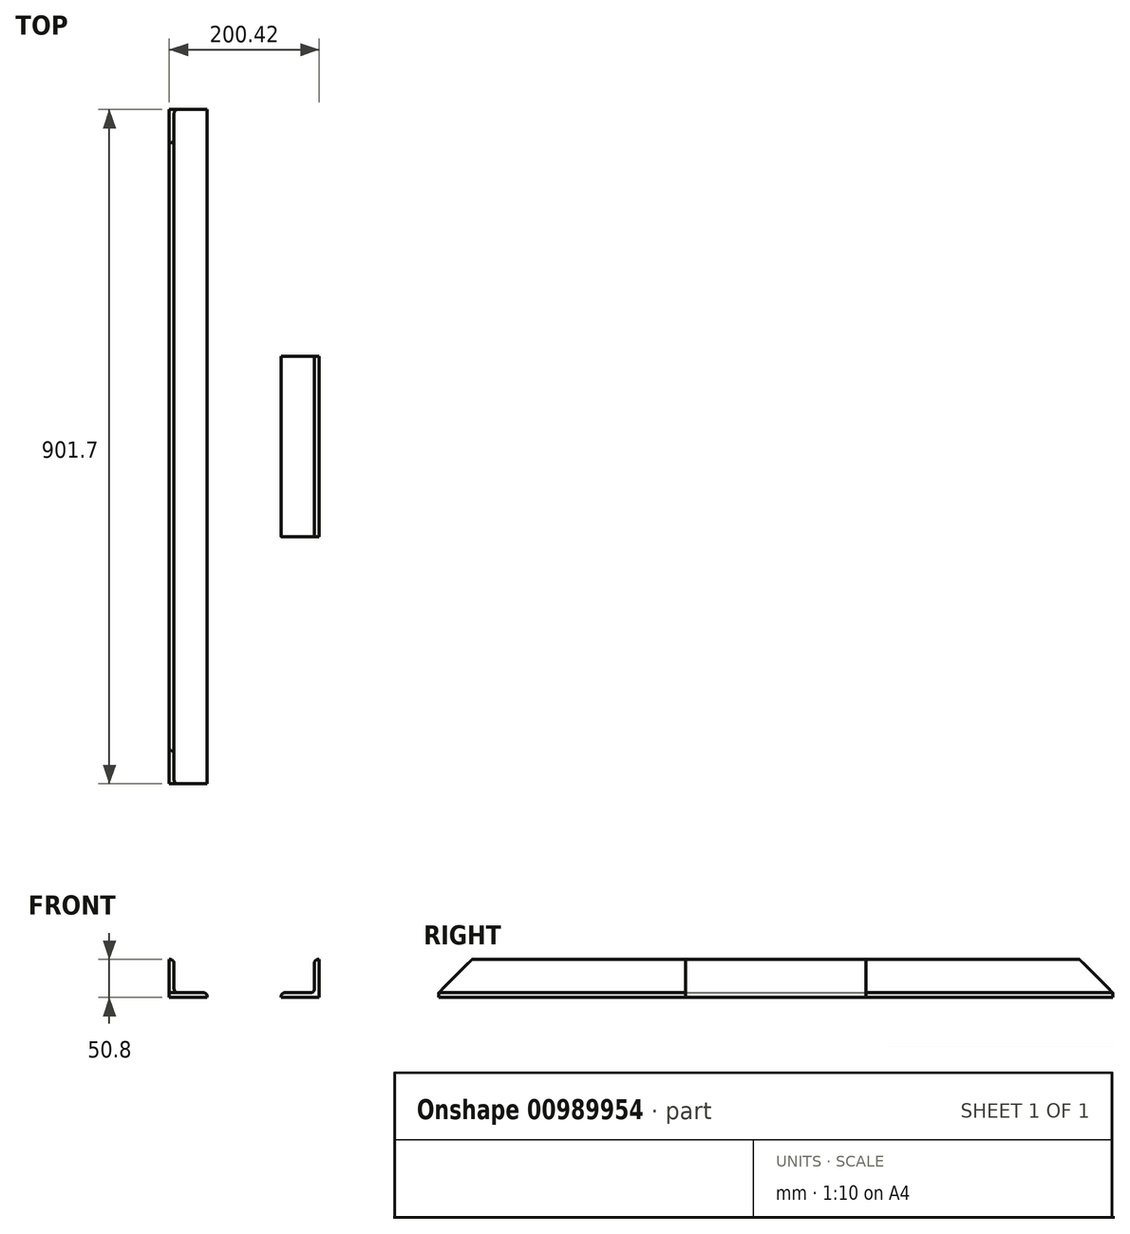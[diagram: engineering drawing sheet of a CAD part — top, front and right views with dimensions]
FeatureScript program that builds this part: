
annotation { "Feature Type Name" : "Feature", "Feature Type Description" : "" }
export const myFeature = defineFeature(function(context is Context, id is Id, definition is map)
    precondition{}
    {
        {
            var Q0;
            Q0=qCreatedBy(makeId("Front.planeOp"),FACE);
            var sketch = newSketch(context, id + "F0", { "sketchPlane" : qUnion([Q0])});
            skLineSegment(sketch, "E0.bottom", {"start": v(25.4, -25.4) * mm, "end": v(-25.4, -25.4) * mm});
            skLineSegment(sketch, "E0.top", {"start": v(-19.05, 25.4) * mm, "end": v(-25.4, 25.4) * mm});
            skLineSegment(sketch, "E0.left", {"start": v(25.4, -25.4) * mm, "end": v(25.4, -19.05) * mm});
            skLineSegment(sketch, "E0.right", {"start": v(-25.4, -25.4) * mm, "end": v(-25.4, 25.4) * mm});
            skPoint(sketch, "E0.middle", {"position": v(0, 0) * mm});
            skLineSegment(sketch, "E1.0", {"start": v(-19.05, -19.05) * mm, "end": v(-19.05, 25.4) * mm});
            skLineSegment(sketch, "E2.0", {"start": v(25.4, -19.05) * mm, "end": v(-19.05, -19.05) * mm});
            skPoint(sketch, "E3.orphan", {"position": v(25.4, 25.4) * mm});
            skLineSegment(sketch, "E4", {"start": v(74.8, 75.28) * mm, "end": v(74.8, -68.93) * mm});
            skLineSegment(sketch, "E5.MirrorCS", {"start": v(168.67, 25.4) * mm, "end": v(175.02, 25.4) * mm});
            skLineSegment(sketch, "E6.MirrorCS", {"start": v(124.22, -25.4) * mm, "end": v(124.22, -19.05) * mm});
            skPoint(sketch, "E7.MirrorP", {"position": v(124.22, 25.4) * mm});
            skLineSegment(sketch, "E8.MirrorCS", {"start": v(124.22, -25.4) * mm, "end": v(175.02, -25.4) * mm});
            skLineSegment(sketch, "E9.MirrorCS", {"start": v(168.67, -19.05) * mm, "end": v(168.67, 25.4) * mm});
            skLineSegment(sketch, "E10.MirrorCS", {"start": v(124.22, -19.05) * mm, "end": v(168.67, -19.05) * mm});
            skLineSegment(sketch, "E11.MirrorCS", {"start": v(175.02, -25.4) * mm, "end": v(175.02, 25.4) * mm});
            skPoint(sketch, "E12.MirrorP", {"position": v(149.62, 0) * mm});
            skSolve(sketch);
        }
        {
            var Q0;
            Q0=makeQuery(id+"F0.imprint","IMPRINT",FACE,{"disambiguationData":[TD([[makeQuery(id+"F0.imprint","IMPRINT",EDGE,{"derivedFrom":sQuery(id+"F0.wireOp",EDGE,"E0.bottom")}),-1.0]])]});
            extrude(context, id + "F1", {"entities" : qUnion([Q0]), "endBound" : BoundingType.SYMMETRIC, "depth" : 901.7 * mm, "offsetDistance" : 25.4 * mm});
        }
        {
            var Q0;
            Q0=makeQuery(id+"F0.imprint","IMPRINT",FACE,{"disambiguationData":[TD([[makeQuery(id+"F0.imprint","IMPRINT",EDGE,{"derivedFrom":sQuery(id+"F0.wireOp",EDGE,"E5.MirrorCS")}),-1.0]])]});
            extrude(context, id + "F2", {"entities" : qUnion([Q0]), "endBound" : BoundingType.SYMMETRIC, "depth" : 241.3 * mm, "offsetDistance" : 25.4 * mm});
        }
        {
            var Q0;
            Q0=makeQuery(id+"F1.opExtrude","SWEPT_FACE",FACE,{"disambiguationData":[OSD([sQuery(id+"F0.wireOp",EDGE,"E1.0")])]});
            var sketch = newSketch(context, id + "F3", { "sketchPlane" : qUnion([Q0])});
            skPoint(sketch, "E13.0", {"position": v(-450.85, -19.05) * mm});
            skPoint(sketch, "E14.0", {"position": v(-450.85, 25.4) * mm});
            skLineSegment(sketch, "E15", {"start": v(-450.85, -19.05) * mm, "end": v(-450.85, 25.4) * mm});
            skLineSegment(sketch, "E16", {"start": v(-450.85, 25.4) * mm, "end": v(-406.4, 25.4) * mm});
            skLineSegment(sketch, "E17", {"start": v(-406.4, 25.4) * mm, "end": v(-450.85, -19.05) * mm});
            skLineSegment(sketch, "E18.MirrorCS", {"start": v(406.4, 25.4) * mm, "end": v(450.85, -19.05) * mm});
            skLineSegment(sketch, "E19.MirrorCS", {"start": v(450.85, 25.4) * mm, "end": v(406.4, 25.4) * mm});
            skLineSegment(sketch, "E20.MirrorCS", {"start": v(450.85, -19.05) * mm, "end": v(450.85, 25.4) * mm});
            skSolve(sketch);
        }
        {
            var Q0;
            Q0 = qSketchRegion(id + "F3", true);
            extrude(context, id + "F4", {"entities" : qUnion([Q0]), "operationType" : NewBodyOperationType.REMOVE, "oppositeDirection" : true, "depth" : 25.4 * mm, "offsetDistance" : 25.4 * mm});
        }
        {
            var Q0;
            Q0=makeQuery(id+"F1.opExtrude","SWEPT_EDGE",EDGE,{"disambiguationData":[OSD([sQuery(id+"F0.wireOp",EDGE,"E1.0"),sQuery(id+"F0.wireOp",EDGE,"E2.0")])]});
            var Q1;
            Q1=makeQuery(id+"F1.opExtrude","SWEPT_EDGE",EDGE,{"disambiguationData":[OSD([sQuery(id+"F0.wireOp",EDGE,"E0.top"),sQuery(id+"F0.wireOp",EDGE,"E1.0")])]});
            var Q2;
            Q2=makeQuery(id+"F1.opExtrude","SWEPT_EDGE",EDGE,{"disambiguationData":[OSD([sQuery(id+"F0.wireOp",EDGE,"E0.left"),sQuery(id+"F0.wireOp",EDGE,"E2.0")])]});
            var Q3;
            Q3=makeQuery(id+"F2.opExtrude","SWEPT_EDGE",EDGE,{"disambiguationData":[OSD([sQuery(id+"F0.wireOp",EDGE,"E9.MirrorCS"),sQuery(id+"F0.wireOp",EDGE,"E10.MirrorCS")])]});
            var Q4;
            Q4=makeQuery(id+"F2.opExtrude","SWEPT_EDGE",EDGE,{"disambiguationData":[OSD([sQuery(id+"F0.wireOp",EDGE,"E6.MirrorCS"),sQuery(id+"F0.wireOp",EDGE,"E10.MirrorCS")])]});
            var Q5;
            Q5=makeQuery(id+"F2.opExtrude","SWEPT_EDGE",EDGE,{"disambiguationData":[OSD([sQuery(id+"F0.wireOp",EDGE,"E5.MirrorCS"),sQuery(id+"F0.wireOp",EDGE,"E9.MirrorCS")])]});
            fillet(context, id + "F5", {"entities" : qUnion([Q0, Q1, Q2, Q3, Q4, Q5]), "radius" : 5.08 * mm, "tangentPropagation" : true, "allowEdgeOverflow" : false});
        }
    });
